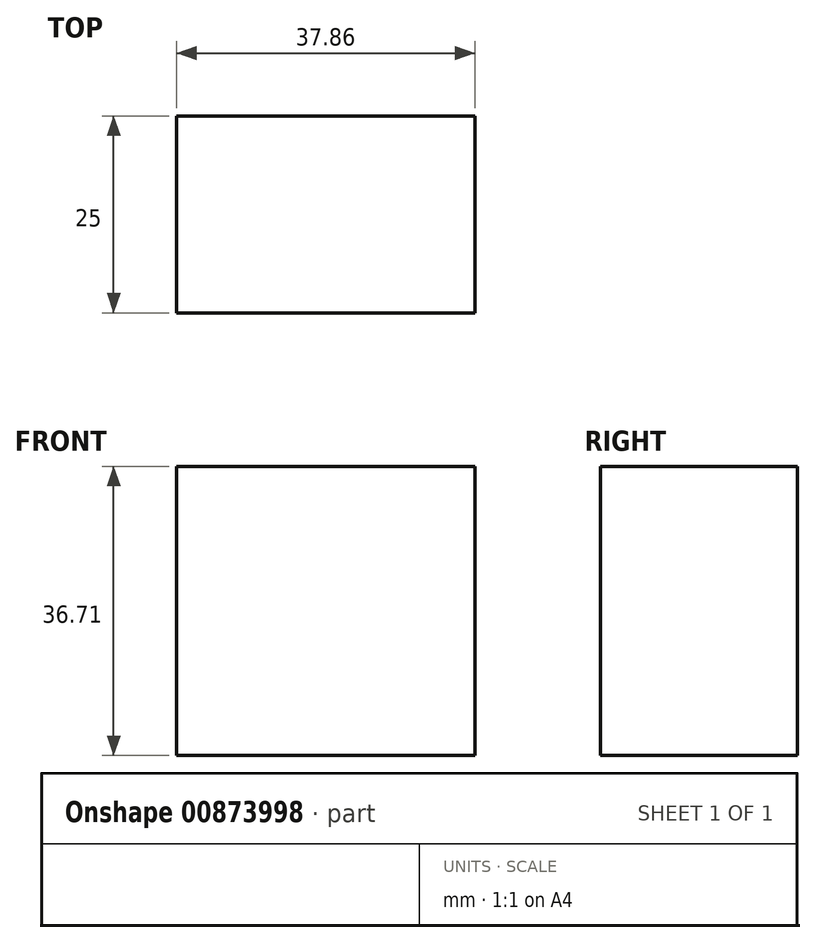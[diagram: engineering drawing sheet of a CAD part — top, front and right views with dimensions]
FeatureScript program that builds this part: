
annotation { "Feature Type Name" : "Feature", "Feature Type Description" : "" }
export const myFeature = defineFeature(function(context is Context, id is Id, definition is map)
    precondition{}
    {
        {
            var Q0;
            Q0=qCreatedBy(makeId("Front.planeOp"),FACE);
            var sketch = newSketch(context, id + "F0", { "sketchPlane" : qUnion([Q0])});
            skLineSegment(sketch, "E0.bottom", {"start": v(-242.38, 41.48) * mm, "end": v(-204.52, 41.48) * mm});
            skLineSegment(sketch, "E0.top", {"start": v(-242.38, 4.77) * mm, "end": v(-204.52, 4.77) * mm});
            skLineSegment(sketch, "E0.left", {"start": v(-242.38, 41.48) * mm, "end": v(-242.38, 4.77) * mm});
            skLineSegment(sketch, "E0.right", {"start": v(-204.52, 41.48) * mm, "end": v(-204.52, 4.77) * mm});
            skLineSegment(sketch, "E1.1.0.0", {"start": v(-164.78, 41.48) * mm, "end": v(-164.78, 4.77) * mm});
            skLineSegment(sketch, "E1.1.0.1", {"start": v(-164.78, 41.48) * mm, "end": v(-126.92, 41.48) * mm});
            skLineSegment(sketch, "E1.1.0.2", {"start": v(-126.92, 41.48) * mm, "end": v(-126.92, 4.77) * mm});
            skLineSegment(sketch, "E1.1.0.3", {"start": v(-164.78, 4.77) * mm, "end": v(-126.92, 4.77) * mm});
            skLineSegment(sketch, "E1.2.0.0", {"start": v(-87.18, 41.48) * mm, "end": v(-87.18, 4.77) * mm});
            skLineSegment(sketch, "E1.2.0.1", {"start": v(-87.18, 41.48) * mm, "end": v(-49.32, 41.48) * mm});
            skLineSegment(sketch, "E1.2.0.2", {"start": v(-49.32, 41.48) * mm, "end": v(-49.32, 4.77) * mm});
            skLineSegment(sketch, "E1.2.0.3", {"start": v(-87.18, 4.77) * mm, "end": v(-49.32, 4.77) * mm});
            skLineSegment(sketch, "E1.direction1", {"start": v(-242.38, 4.77) * mm, "end": v(-164.78, 4.77) * mm, "construction": true});
            skSolve(sketch);
        }
        {
            var Q0;
            Q0=makeQuery(id+"F0.imprint","IMPRINT",FACE,{"disambiguationData":[TD([[makeQuery(id+"F0.imprint","IMPRINT",EDGE,{"derivedFrom":sQuery(id+"F0.wireOp",EDGE,"E0.bottom")}),-1.0]])]});
            var Q1;
            Q1=makeQuery(id+"F0.imprint","IMPRINT",FACE,{"disambiguationData":[TD([[makeQuery(id+"F0.imprint","IMPRINT",EDGE,{"derivedFrom":sQuery(id+"F0.wireOp",EDGE,"E1.1.0.0")}),-1.0]])]});
            var Q2;
            Q2=makeQuery(id+"F0.imprint","IMPRINT",FACE,{"disambiguationData":[TD([[makeQuery(id+"F0.imprint","IMPRINT",EDGE,{"derivedFrom":sQuery(id+"F0.wireOp",EDGE,"E1.2.0.0")}),-1.0]])]});
            extrude(context, id + "F1", {"entities" : qUnion([Q0, Q1, Q2]), "depth" : 25 * mm, "offsetDistance" : 25 * mm});
        }
    });
